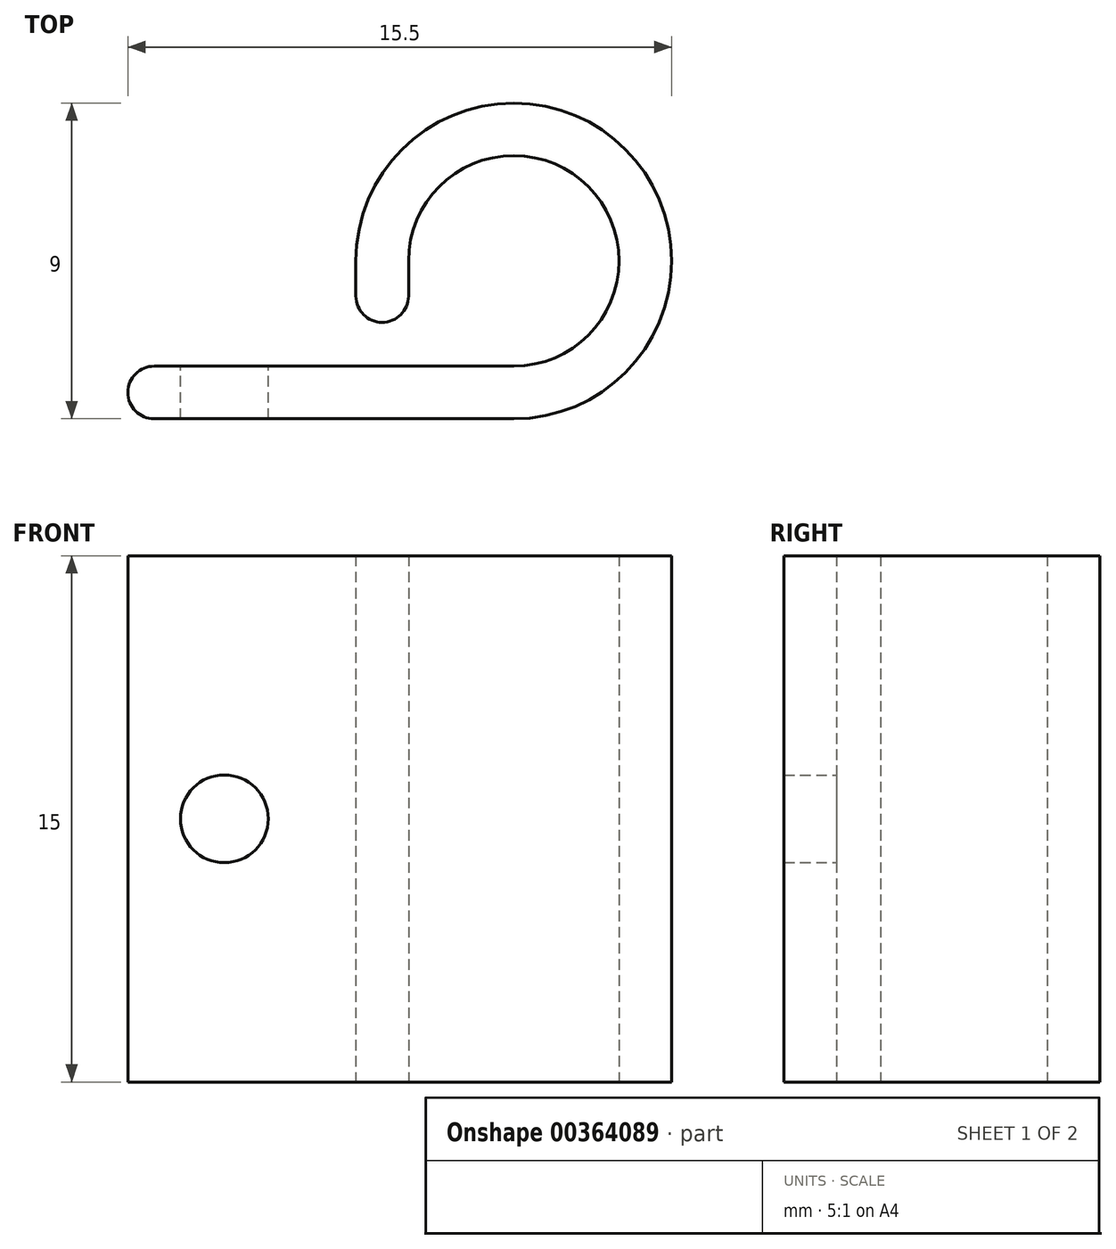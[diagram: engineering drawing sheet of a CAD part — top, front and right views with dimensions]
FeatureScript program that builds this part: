
annotation { "Feature Type Name" : "Feature", "Feature Type Description" : "" }
export const myFeature = defineFeature(function(context is Context, id is Id, definition is map)
    precondition{}
    {
        {
            var Q0;
            Q0=qCreatedBy(makeId("Top.planeOp"),FACE);
            var sketch = newSketch(context, id + "F0", { "sketchPlane" : qUnion([Q0])});
            skArc(sketch, "E0", {"start": v(0, -3) * mm, "mid": v(2.12, 2.12) * mm, "end": v(-3, 0) * mm});
            skLineSegment(sketch, "E1", {"start": v(0, -3) * mm, "end": v(-11, -3) * mm});
            skArc(sketch, "E2", {"start": v(0, -4.5) * mm, "mid": v(3.18, 3.18) * mm, "end": v(-4.5, 0) * mm});
            skLineSegment(sketch, "E3", {"start": v(0, -4.5) * mm, "end": v(-11, -4.5) * mm});
            skLineSegment(sketch, "E4", {"start": v(-11, -3) * mm, "end": v(-11, -4.5) * mm});
            skLineSegment(sketch, "E5", {"start": v(-3, 0) * mm, "end": v(-4.5, 0) * mm, "construction": true});
            skLineSegment(sketch, "E6", {"start": v(0, -3) * mm, "end": v(0, -1.5) * mm, "construction": true});
            skArc(sketch, "E7", {"start": v(-4.5, -1) * mm, "mid": v(-3.75, -1.75) * mm, "end": v(-3, -1) * mm});
            skLineSegment(sketch, "E8", {"start": v(-3.75, 0) * mm, "end": v(-3.75, -62.4) * mm, "construction": true});
            skLineSegment(sketch, "E9", {"start": v(-4.5, 0) * mm, "end": v(-4.5, -1) * mm});
            skLineSegment(sketch, "E10", {"start": v(-3, 0) * mm, "end": v(-3, -1) * mm});
            skSolve(sketch);
        }
        {
            var Q0;
            Q0 = qSketchRegion(id + "F0", true);
            extrude(context, id + "F1", {"entities" : qUnion([Q0]), "depth" : 15 * mm});
        }
        {
            var Q0;
            Q0=makeQuery(id+"F1.opExtrude","SWEPT_EDGE",EDGE,{"disambiguationData":[OSD([sQuery(id+"F0.wireOp",EDGE,"E1"),sQuery(id+"F0.wireOp",EDGE,"1aaa02f7-7a2d-470d-9015-888008587281.trimOffspring")])]});
            var Q1;
            Q1=makeQuery(id+"F1.opExtrude","SWEPT_EDGE",EDGE,{"disambiguationData":[OSD([sQuery(id+"F0.wireOp",EDGE,"E3"),sQuery(id+"F0.wireOp",EDGE,"1aaa02f7-7a2d-470d-9015-888008587281.trimOffspring")])]});
            fillet(context, id + "F2", {"entities" : qUnion([Q0, Q1]), "radius" : .75 * mm, "allowEdgeOverflow" : false});
        }
        {
            var Q0;
            Q0=makeQuery(id+"F1.opExtrude","SWEPT_FACE",FACE,{"disambiguationData":[OSD([sQuery(id+"F0.wireOp",EDGE,"E1")])]});
            var sketch = newSketch(context, id + "F3", { "sketchPlane" : qUnion([Q0])});
            skCircle(sketch, "E11", {"center": v(8.25, 7.5) * mm, "radius": 1.25 * mm});
            skSolve(sketch);
        }
        {
            var Q0;
            Q0 = qSketchRegion(id + "F3", true);
            extrude(context, id + "F4", {"entities" : qUnion([Q0]), "operationType" : NewBodyOperationType.REMOVE, "oppositeDirection" : true, "depth" : 8.2 * mm});
        }
    });
